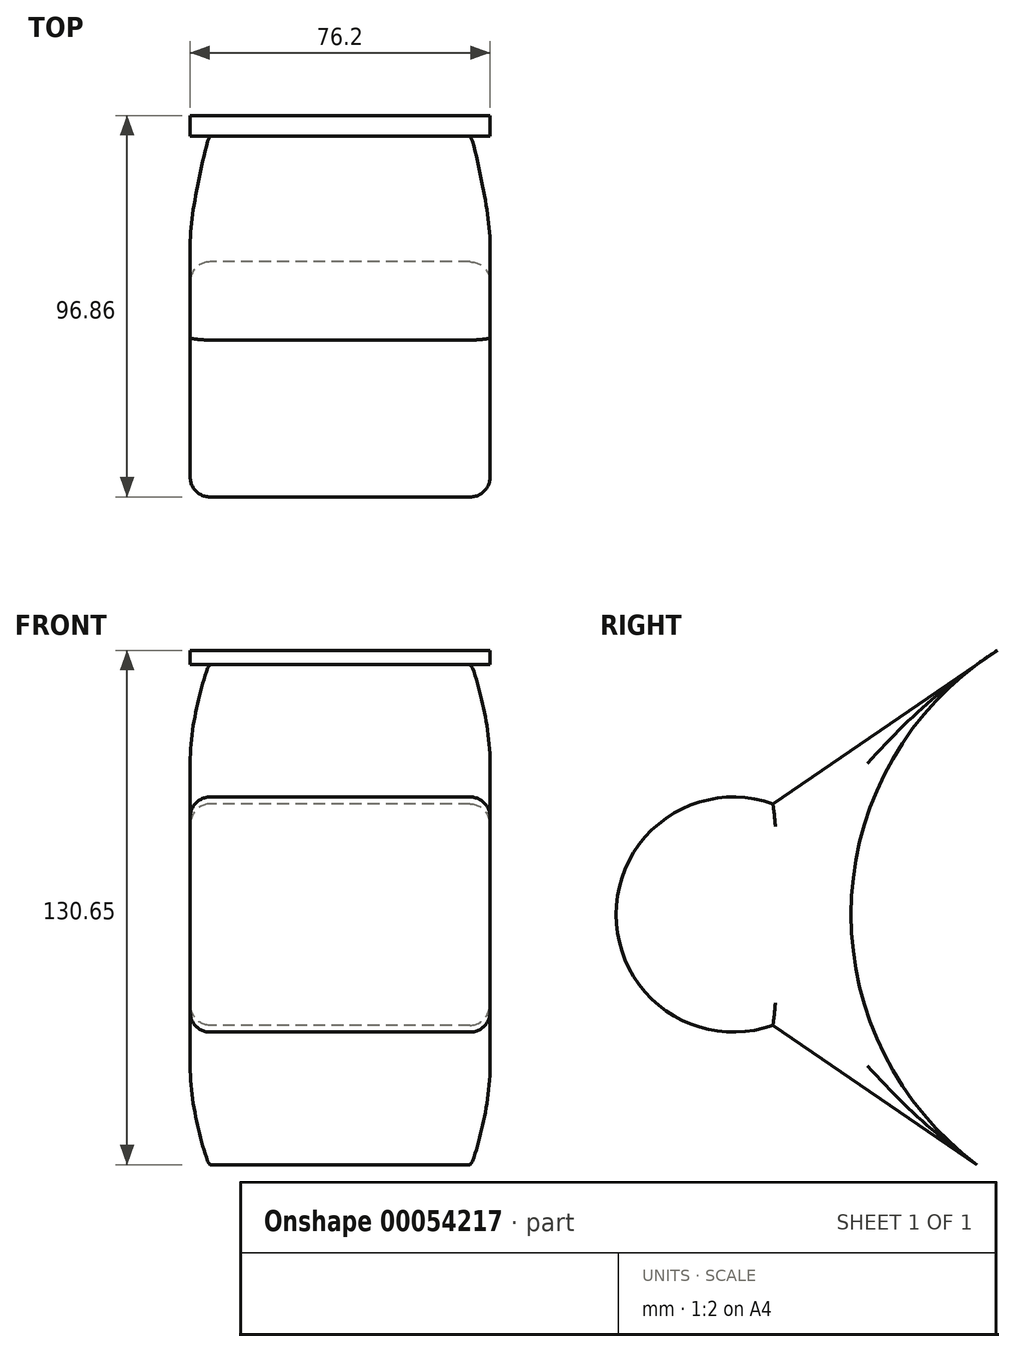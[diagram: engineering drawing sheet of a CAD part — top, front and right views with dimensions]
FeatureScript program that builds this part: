
annotation { "Feature Type Name" : "Feature", "Feature Type Description" : "" }
export const myFeature = defineFeature(function(context is Context, id is Id, definition is map)
    precondition{}
    {
        {
            var Q0;
            Q0=qCreatedBy(makeId("Right.planeOp"),FACE);
            var sketch = newSketch(context, id + "F0", { "sketchPlane" : qUnion([Q0])});
            skCircle(sketch, "E0", {"center": v(-59.2, 0) * mm, "radius": 29.87 * mm});
            skCircle(sketch, "E1", {"center": v(49.86, 0) * mm, "radius": 79.2 * mm});
            skLineSegment(sketch, "E2", {"start": v(7.79, 67.1) * mm, "end": v(-49.2, 28.14) * mm});
            skLineSegment(sketch, "E3", {"start": v(7.79, -67.1) * mm, "end": v(-49.2, -28.14) * mm});
            skSolve(sketch);
        }
        {
            var Q0;
            {var subQ0=sQuery(id+"F0.wireOp",EDGE,"E2");var subQ1=sQuery(id+"F0.wireOp",EDGE,"E1");var subQ3=makeQuery(id+"F0.imprint","INTERSECT",VERTEX,{"disambiguationData":[OD(1.0)],"derivedFrom":[subQ1,subQ0]});Q0=makeQuery(id+"F0.imprint","IMPRINT",FACE,{"disambiguationData":[TD([[makeQuery(id+"F0.imprint","IMPRINT",EDGE,{"disambiguationData":[TD([[subQ3,-1.0]])],"derivedFrom":subQ1}),1.0]])]});}
            var Q1;
            {var subQ0=sQuery(id+"F0.wireOp",EDGE,"E3");var subQ1=sQuery(id+"F0.wireOp",EDGE,"E0");var subQ2=makeQuery(id+"F0.imprint","INTERSECT",VERTEX,{"derivedFrom":[subQ1,subQ0]});Q1=makeQuery(id+"F0.imprint","IMPRINT",FACE,{"disambiguationData":[TD([[makeQuery(id+"F0.imprint","IMPRINT",EDGE,{"disambiguationData":[TD([[subQ2,-1.0]])],"derivedFrom":subQ1}),-1.0]])]});}
            var Q2;
            {var subQ0=sQuery(id+"F0.wireOp",EDGE,"E0");var subQ1=makeQuery(id+"F0.imprint","INTERSECT",VERTEX,{"derivedFrom":[subQ0,sQuery(id+"F0.wireOp",EDGE,"E2")]});Q2=makeQuery(id+"F0.imprint","IMPRINT",FACE,{"disambiguationData":[TD([[makeQuery(id+"F0.imprint","IMPRINT",EDGE,{"disambiguationData":[TD([[subQ1,1.0]])],"derivedFrom":subQ0}),1.0]])]});}
            var Q3;
            {var subQ0=sQuery(id+"F0.wireOp",EDGE,"E2");var subQ1=sQuery(id+"F0.wireOp",EDGE,"E0");var subQ2=makeQuery(id+"F0.imprint","INTERSECT",VERTEX,{"derivedFrom":[subQ1,subQ0]});Q3=makeQuery(id+"F0.imprint","IMPRINT",FACE,{"disambiguationData":[TD([[makeQuery(id+"F0.imprint","IMPRINT",EDGE,{"disambiguationData":[TD([[subQ2,1.0]])],"derivedFrom":subQ1}),-1.0]])]});}
            extrude(context, id + "F1", {"entities" : qUnion([Q0, Q1, Q2, Q3]), "depth" : 76.2 * mm});
        }
        {
            var Q0;
            Q0=makeQuery(id+"F1.opExtrude","CAP_EDGE",EDGE,{"disambiguationData":[OSD([sQuery(id+"F0.wireOp",EDGE,"E0")])],"isStart":false});
            fillet(context, id + "F2", {"entities" : qUnion([Q0]), "radius" : 5.08 * mm, "tangentPropagation" : true, "allowEdgeOverflow" : false});
        }
        {
            var Q0;
            Q0=makeQuery(id+"F1.opExtrude","CAP_EDGE",EDGE,{"disambiguationData":[OSD([sQuery(id+"F0.wireOp",EDGE,"E2")])],"isStart":false});
            var Q1;
            Q1=makeQuery(id+"F1.opExtrude","CAP_EDGE",EDGE,{"disambiguationData":[OSD([sQuery(id+"F0.wireOp",EDGE,"E1")])],"isStart":false});
            var Q2;
            Q2=makeQuery(id+"F1.opExtrude","CAP_EDGE",EDGE,{"disambiguationData":[OSD([sQuery(id+"F0.wireOp",EDGE,"E3")])],"isStart":false});
            fillet(context, id + "F3", {"entities" : qUnion([Q0, Q1, Q2]), "radius" : 5.08 * mm, "tangentPropagation" : true, "allowEdgeOverflow" : false});
        }
        {
            var Q0;
            Q0=makeQuery(id+"F1.opExtrude","CAP_EDGE",EDGE,{"disambiguationData":[OSD([sQuery(id+"F0.wireOp",EDGE,"E0")])],"isStart":true});
            var Q1;
            Q1=makeQuery(id+"F1.opExtrude","CAP_EDGE",EDGE,{"disambiguationData":[OSD([sQuery(id+"F0.wireOp",EDGE,"E3")])],"isStart":true});
            var Q2;
            Q2=makeQuery(id+"F1.opExtrude","CAP_EDGE",EDGE,{"disambiguationData":[OSD([sQuery(id+"F0.wireOp",EDGE,"E2")])],"isStart":true});
            var Q3;
            Q3=makeQuery(id+"F1.opExtrude","CAP_EDGE",EDGE,{"disambiguationData":[OSD([sQuery(id+"F0.wireOp",EDGE,"E1")])],"isStart":true});
            fillet(context, id + "F4", {"entities" : qUnion([Q0, Q1, Q2, Q3]), "radius" : 5.08 * mm, "tangentPropagation" : true, "allowEdgeOverflow" : false});
        }
    });
